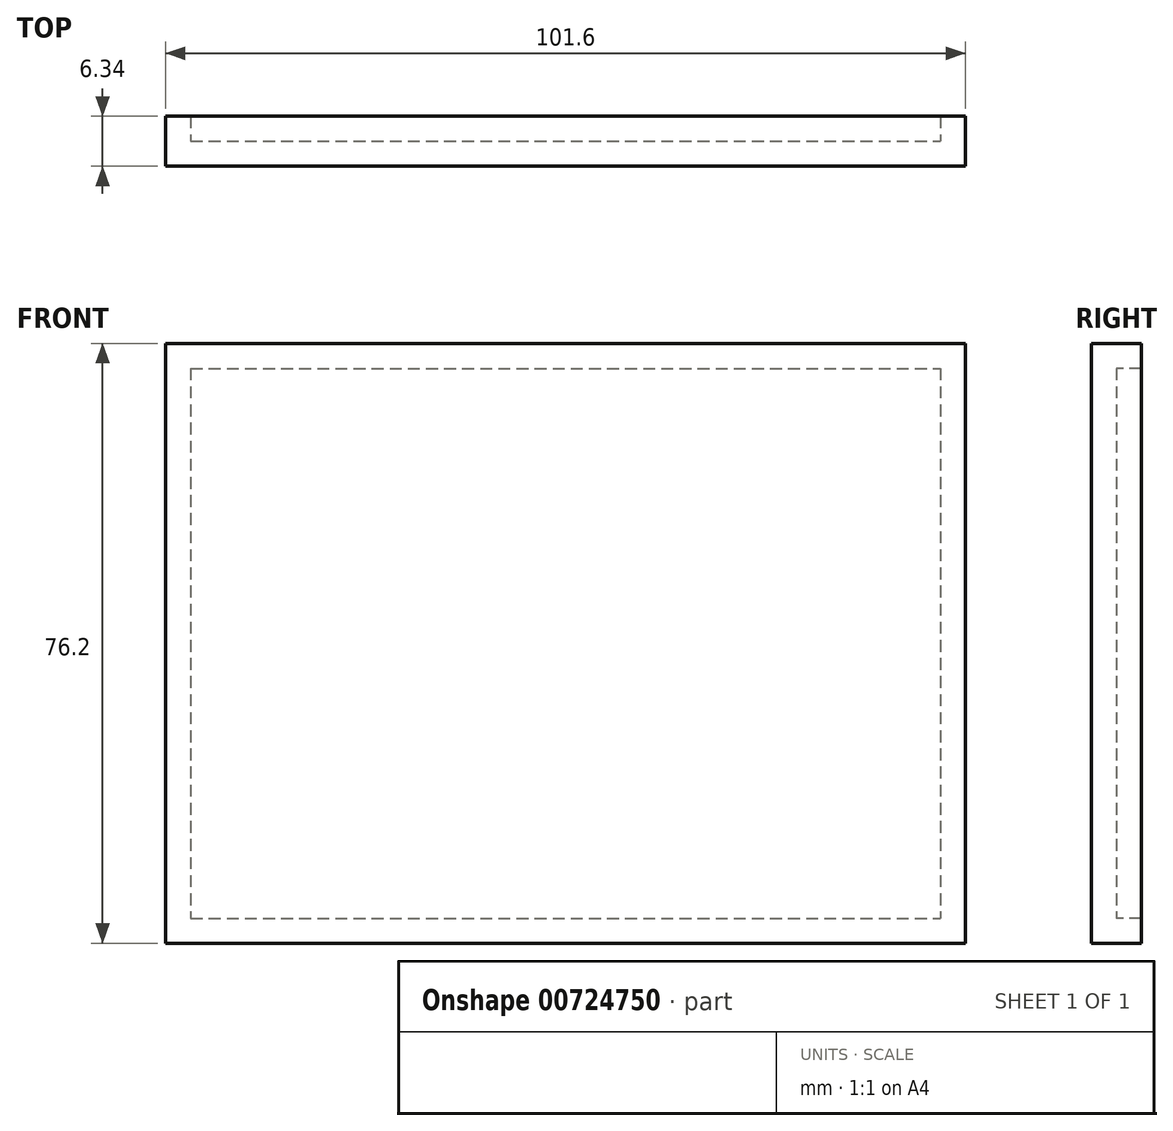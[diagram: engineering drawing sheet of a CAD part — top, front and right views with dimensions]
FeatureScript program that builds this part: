
annotation { "Feature Type Name" : "Feature", "Feature Type Description" : "" }
export const myFeature = defineFeature(function(context is Context, id is Id, definition is map)
    precondition{}
    {
        {
            var Q0;
            Q0=qCreatedBy(makeId("Front.planeOp"),FACE);
            var sketch = newSketch(context, id + "F0", { "sketchPlane" : qUnion([Q0])});
            skLineSegment(sketch, "E0.bottom", {"start": v(50.8, 38.1) * mm, "end": v(-50.8, 38.1) * mm});
            skLineSegment(sketch, "E0.top", {"start": v(50.8, -38.1) * mm, "end": v(-50.8, -38.1) * mm});
            skLineSegment(sketch, "E0.left", {"start": v(50.8, 38.1) * mm, "end": v(50.8, -38.1) * mm});
            skLineSegment(sketch, "E0.right", {"start": v(-50.8, 38.1) * mm, "end": v(-50.8, -38.1) * mm});
            skPoint(sketch, "E0.middle", {"position": v(0, 0) * mm});
            skSolve(sketch);
        }
        {
            var Q0;
            Q0=qCreatedBy(makeId("Front.planeOp"),FACE);
            var sketch = newSketch(context, id + "F1", { "sketchPlane" : qUnion([Q0])});
            skLineSegment(sketch, "E1.bottom", {"start": v(-47.62, 34.93) * mm, "end": v(47.63, 34.93) * mm});
            skLineSegment(sketch, "E1.top", {"start": v(-47.63, -34.93) * mm, "end": v(47.62, -34.93) * mm});
            skLineSegment(sketch, "E1.left", {"start": v(-47.63, 34.93) * mm, "end": v(-47.63, -34.93) * mm});
            skLineSegment(sketch, "E1.right", {"start": v(47.63, 34.93) * mm, "end": v(47.63, -34.93) * mm});
            skPoint(sketch, "E1.middle", {"position": v(0, 0) * mm});
            skSolve(sketch);
        }
        {
            var Q0;
            Q0 = qSketchRegion(id + "F0", true);
            extrude(context, id + "F2", {"entities" : qUnion([Q0]), "endBound" : BoundingType.SYMMETRIC, "depth" : 6.35 * mm, "offsetDistance" : 25.4 * mm});
        }
        {
            var Q0;
            Q0 = qSketchRegion(id + "F1", true);
            extrude(context, id + "F3", {"entities" : qUnion([Q0]), "operationType" : NewBodyOperationType.REMOVE, "oppositeDirection" : true, "depth" : 112.52 * mm, "offsetDistance" : 25.4 * mm});
        }
    });
